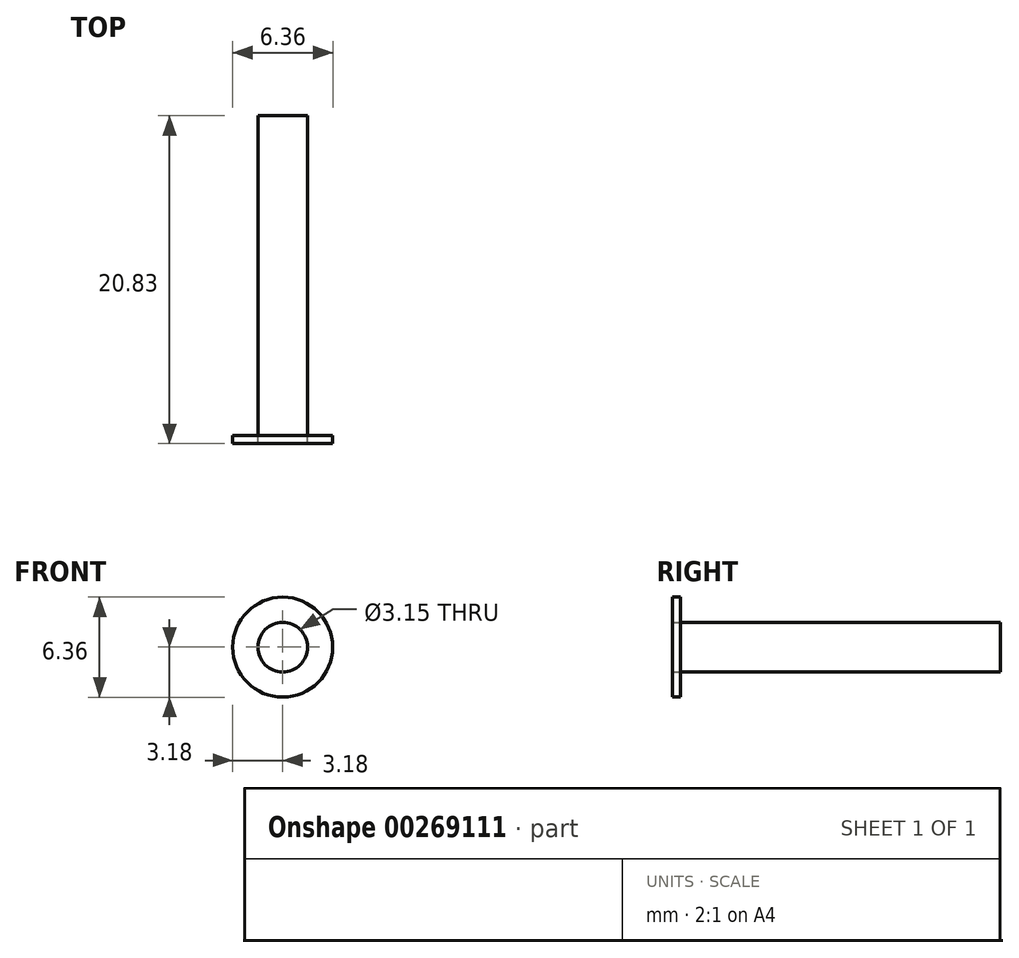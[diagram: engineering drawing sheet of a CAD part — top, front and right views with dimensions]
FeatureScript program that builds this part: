
annotation { "Feature Type Name" : "Feature", "Feature Type Description" : "" }
export const myFeature = defineFeature(function(context is Context, id is Id, definition is map)
    precondition{}
    {
        {
            var Q0;
            Q0=qCreatedBy(makeId("Front.planeOp"),FACE);
            var sketch = newSketch(context, id + "F0", { "sketchPlane" : qUnion([Q0])});
            skCircle(sketch, "E0", {"center": v(0, 0) * mm, "radius": 1.57 * mm});
            skSolve(sketch);
        }
        {
            var Q0;
            Q0=makeQuery(id+"F0.imprint","IMPRINT",FACE,{"disambiguationData":[TD([[makeQuery(id+"F0.imprint","IMPRINT",EDGE,{"derivedFrom":sQuery(id+"F0.wireOp",EDGE,"E0")}),1.0]])]});
            extrude(context, id + "F1", {"entities" : qUnion([Q0]), "depth" : 20.32 * mm});
        }
        {
            var Q0;
            Q0=makeQuery(id+"F1.opExtrude","CAP_FACE",FACE,{"disambiguationData":[OSD([sQuery(id+"F0.wireOp",EDGE,"E0")])],"isStart":false});
            var sketch = newSketch(context, id + "F2", { "sketchPlane" : qUnion([Q0])});
            skCircle(sketch, "E1", {"center": v(0, 0) * mm, "radius": 3.18 * mm});
            skSolve(sketch);
        }
        {
            var Q0;
            Q0=makeQuery(id+"F2.imprint","IMPRINT",FACE,{"disambiguationData":[TD([[makeQuery(id+"F2.imprint","IMPRINT",EDGE,{"derivedFrom":sQuery(id+"F2.wireOp",EDGE,"E1")}),1.0]])]});
            extrude(context, id + "F3", {"entities" : qUnion([Q0]), "depth" : 0.5 * mm});
        }
    });
